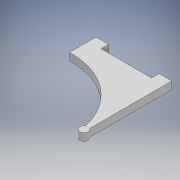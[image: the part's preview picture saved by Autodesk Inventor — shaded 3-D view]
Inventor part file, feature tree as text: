
AUTODESK INVENTOR PART (.ipt)
format: ipt  version: 2017 (Build 210142000, 142)  size: 104,960 bytes
history: native  units: mm
features: extrude x1, sketch x1
ambient origin geometry x8: Origin, YZ Plane, XZ Plane, XY Plane, X Axis, Y Axis, Z Axis, Center Point
bodies: Solide1 (feature_tree)
feature tree (2):
  extrude  "Extrusion1"  Depth=60.0mm
  sketch  "Esquisse1"
